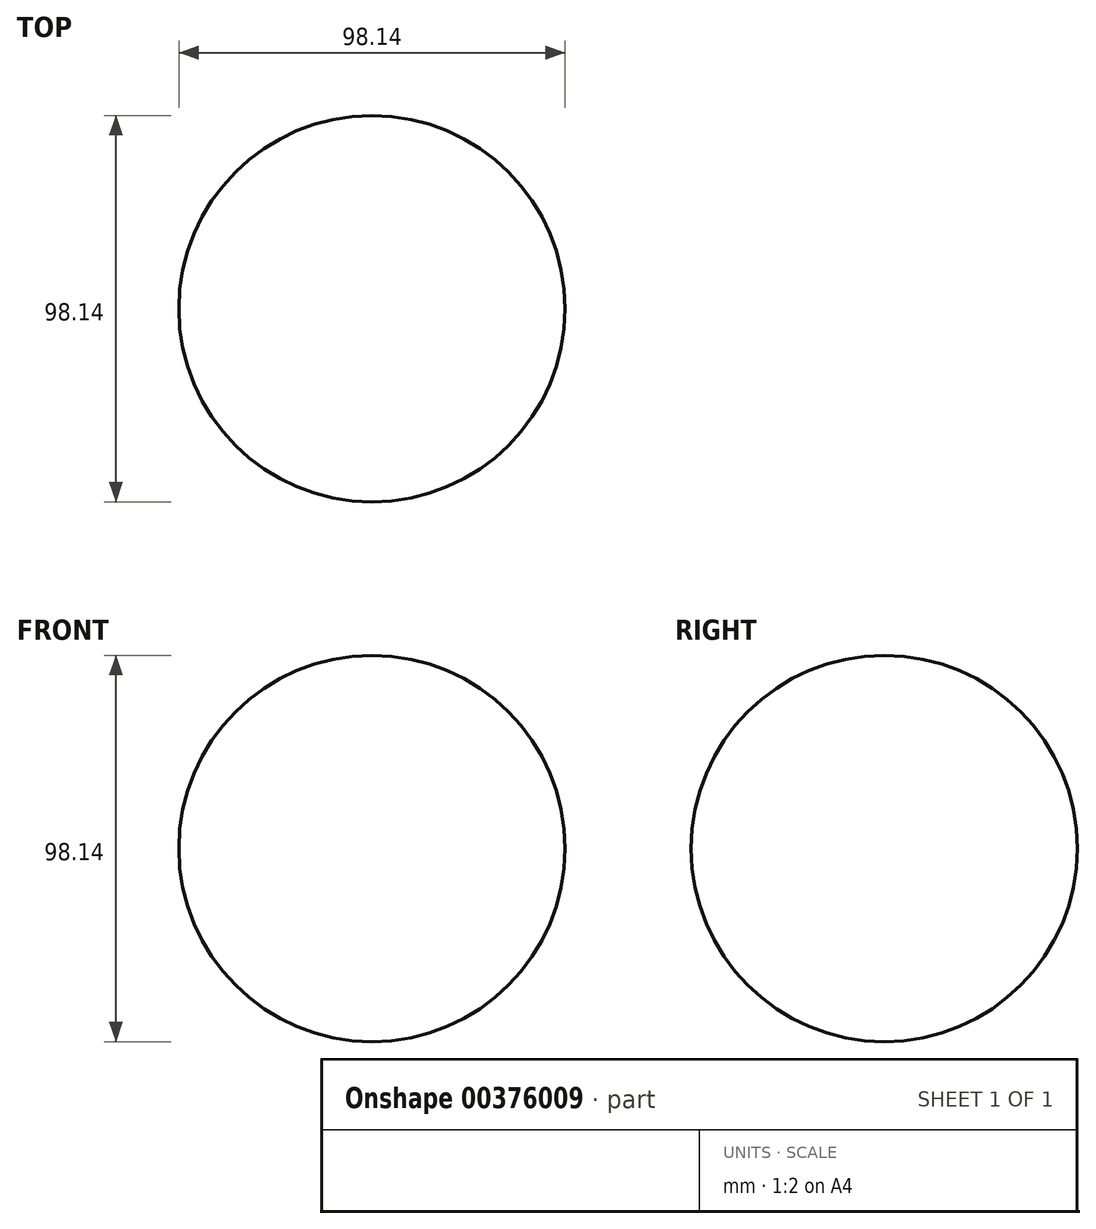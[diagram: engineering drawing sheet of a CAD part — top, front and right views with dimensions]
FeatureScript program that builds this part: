
annotation { "Feature Type Name" : "Feature", "Feature Type Description" : "" }
export const myFeature = defineFeature(function(context is Context, id is Id, definition is map)
    precondition{}
    {
        {
            var Q0;
            Q0=qCreatedBy(makeId("Right.planeOp"),FACE);
            var sketch = newSketch(context, id + "F0", { "sketchPlane" : qUnion([Q0])});
            skCircle(sketch, "E0", {"center": v(0, 0) * mm, "radius": 49.07 * mm});
            skLineSegment(sketch, "E1", {"start": v(0, 0) * mm, "end": v(0, 49.07) * mm});
            skLineSegment(sketch, "E2", {"start": v(0, 49.07) * mm, "end": v(0, -49.07) * mm});
            skSolve(sketch);
        }
        {
            var Q0;
            {var subQ0=sQuery(id+"F0.wireOp",EDGE,"E2");var subQ4=makeQuery(id+"F0.imprint","IMPRINT",VERTEX,{"derivedFrom":subQ0});Q0=makeQuery(id+"F0.imprint","IMPRINT",FACE,{"disambiguationData":[TD([[makeQuery(id+"F0.imprint","IMPRINT",EDGE,{"disambiguationData":[TD([[subQ4,1.0]])],"derivedFrom":subQ0}),1.0]])]});}
            var Q1;
            Q1=sQuery(id+"F0.wireOp",EDGE,"E2");
            revolve(context, id + "F1", {"entities" : qUnion([Q0]), "axis" : qUnion([Q1]), "revolveType" : RevolveType.FULL});
        }
    });
